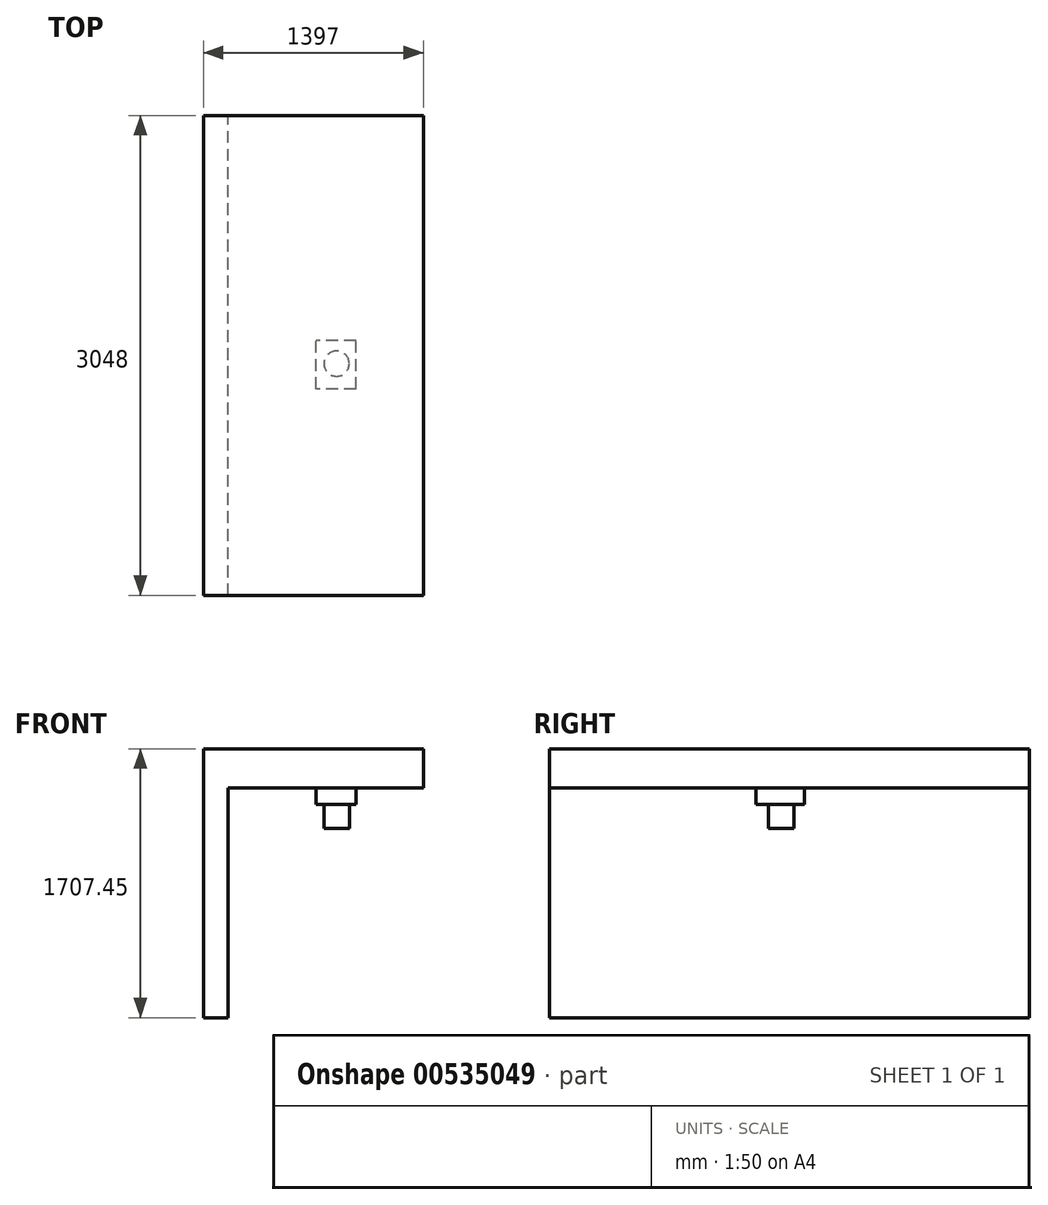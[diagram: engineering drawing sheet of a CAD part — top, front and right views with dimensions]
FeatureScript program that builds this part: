
annotation { "Feature Type Name" : "Feature", "Feature Type Description" : "" }
export const myFeature = defineFeature(function(context is Context, id is Id, definition is map)
    precondition{}
    {
        {
            var Q0;
            Q0=qCreatedBy(makeId("Front.planeOp"),FACE);
            var sketch = newSketch(context, id + "F0", { "sketchPlane" : qUnion([Q0])});
            skLineSegment(sketch, "E0.bottom", {"start": v(-1241.78, -724.17) * mm, "end": v(-1397, -724.17) * mm});
            skLineSegment(sketch, "E0.top", {"start": v(0, 983.28) * mm, "end": v(-1397, 983.28) * mm});
            skLineSegment(sketch, "E0.left", {"start": v(0, 736.37) * mm, "end": v(0, 983.28) * mm});
            skLineSegment(sketch, "E0.right", {"start": v(-1397, -724.17) * mm, "end": v(-1397, 983.28) * mm});
            skLineSegment(sketch, "E1.bottom", {"start": v(0, 736.37) * mm, "end": v(-1241.78, 736.37) * mm});
            skLineSegment(sketch, "E1.right", {"start": v(-1241.78, 736.37) * mm, "end": v(-1241.78, -724.17) * mm});
            skLineSegment(sketch, "E2.bottom", {"start": v(-232.97, 736.37) * mm, "end": v(-445.17, 736.37) * mm});
            skPoint(sketch, "E3.orphan", {"position": v(0, -724.17) * mm});
            skSolve(sketch);
        }
        {
            var Q0;
            Q0=makeQuery(id+"F0.imprint","IMPRINT",FACE,{"disambiguationData":[TD([[makeQuery(id+"F0.imprint","IMPRINT",EDGE,{"derivedFrom":sQuery(id+"F0.wireOp",EDGE,"E0.bottom")}),-1.0]])]});
            extrude(context, id + "F1", {"entities" : qUnion([Q0]), "depth" : 3048 * mm, "offsetDistance" : 25.4 * mm});
        }
        {
            var Q0;
            Q0=makeQuery(id+"F1.opExtrude","SWEPT_FACE",FACE,{"disambiguationData":[OSD([sQuery(id+"F0.wireOp",EDGE,"E1.bottom"),sQuery(id+"F0.wireOp",EDGE,"E2.bottom")])]});
            var sketch = newSketch(context, id + "F2", { "sketchPlane" : qUnion([Q0])});
            skLineSegment(sketch, "E4.bottom", {"start": v(-427.55, 1737.14) * mm, "end": v(-681.37, 1737.14) * mm});
            skLineSegment(sketch, "E4.top", {"start": v(-427.55, 1428.07) * mm, "end": v(-681.37, 1428.07) * mm});
            skLineSegment(sketch, "E4.left", {"start": v(-427.55, 1737.14) * mm, "end": v(-427.55, 1428.07) * mm});
            skLineSegment(sketch, "E4.right", {"start": v(-681.37, 1737.14) * mm, "end": v(-681.37, 1428.07) * mm});
            skSolve(sketch);
        }
        {
            var Q0;
            Q0=makeQuery(id+"F2.imprint","IMPRINT",FACE,{"disambiguationData":[TD([[makeQuery(id+"F2.imprint","IMPRINT",EDGE,{"derivedFrom":sQuery(id+"F2.wireOp",EDGE,"E4.bottom")}),1.0]])]});
            extrude(context, id + "F3", {"entities" : qUnion([Q0]), "operationType" : NewBodyOperationType.ADD, "depth" : 106.68 * mm, "offsetDistance" : 25.4 * mm});
        }
        {
            var Q0;
            Q0=makeQuery(id+"F3.opExtrude","CAP_FACE",FACE,{"disambiguationData":[OSD([sQuery(id+"F2.wireOp",EDGE,"E4.bottom"),sQuery(id+"F2.wireOp",EDGE,"E4.top"),sQuery(id+"F2.wireOp",EDGE,"E4.left"),sQuery(id+"F2.wireOp",EDGE,"E4.right")])],"isStart":false});
            var sketch = newSketch(context, id + "F4", { "sketchPlane" : qUnion([Q0])});
            skCircle(sketch, "E5", {"center": v(-551.25, 1576.1) * mm, "radius": 80.7 * mm});
            skSolve(sketch);
        }
        {
            var Q0;
            Q0=makeQuery(id+"F4.imprint","IMPRINT",FACE,{"disambiguationData":[TD([[makeQuery(id+"F4.imprint","IMPRINT",EDGE,{"derivedFrom":sQuery(id+"F4.wireOp",EDGE,"E5")}),1.0]])]});
            extrude(context, id + "F5", {"entities" : qUnion([Q0]), "operationType" : NewBodyOperationType.ADD, "depth" : 152.4 * mm, "offsetDistance" : 25.4 * mm});
        }
    });
